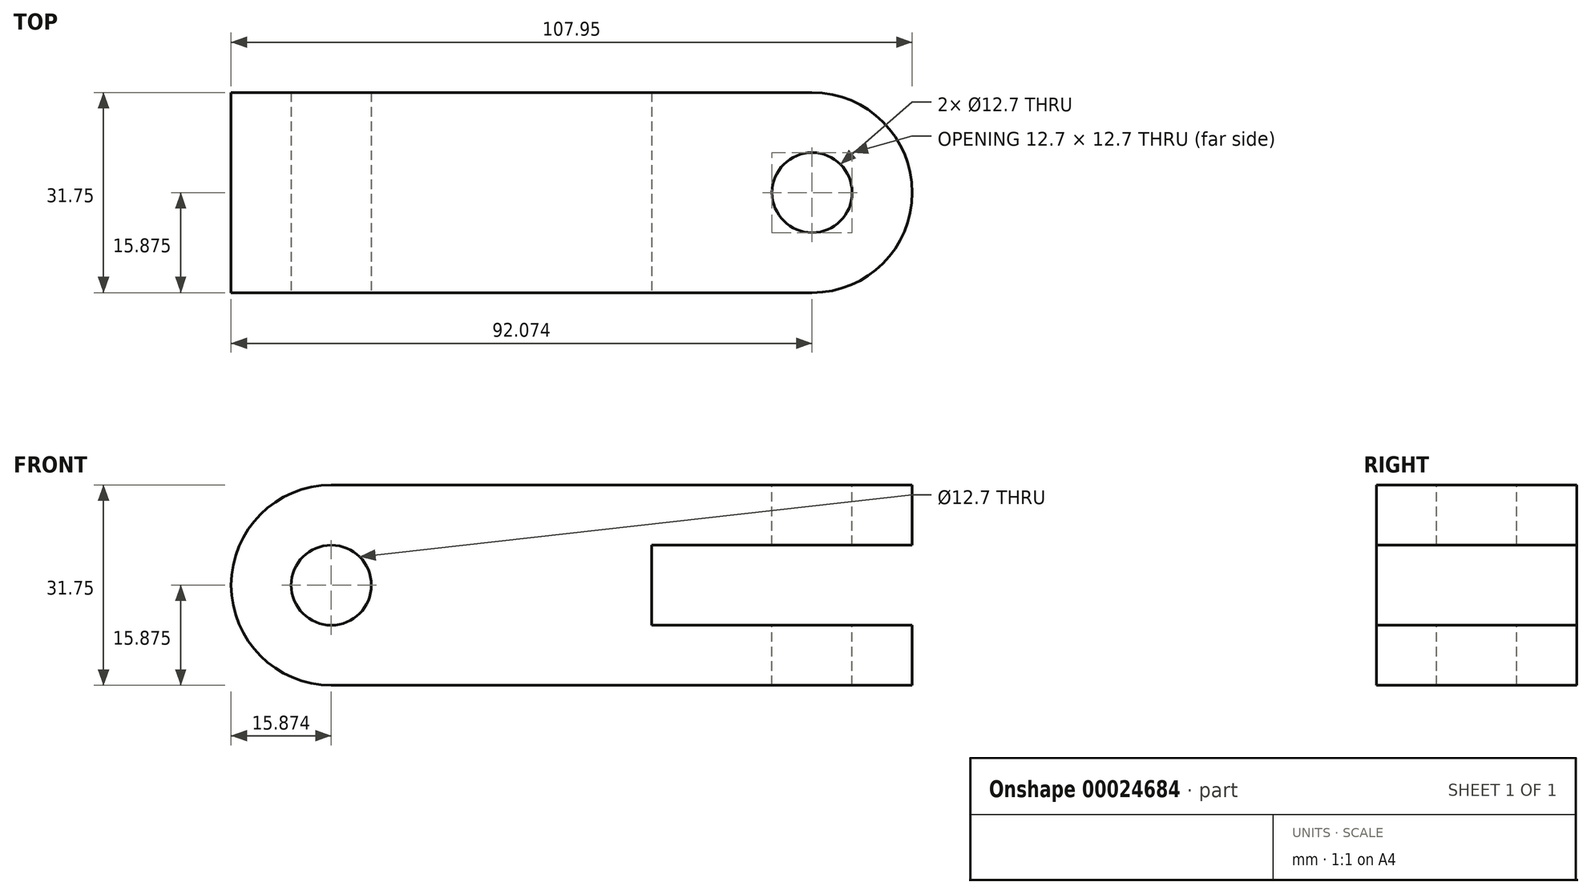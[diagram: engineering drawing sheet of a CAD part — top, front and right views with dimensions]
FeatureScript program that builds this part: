
annotation { "Feature Type Name" : "Feature", "Feature Type Description" : "" }
export const myFeature = defineFeature(function(context is Context, id is Id, definition is map)
    precondition{}
    {
        {
            var Q0;
            Q0=qCreatedBy(makeId("Front.planeOp"),FACE);
            var sketch = newSketch(context, id + "F0", { "sketchPlane" : qUnion([Q0])});
            skLineSegment(sketch, "E0.bottom", {"start": v(-42.47, 14.22) * mm, "end": v(65.48, 14.22) * mm});
            skLineSegment(sketch, "E0.top", {"start": v(-42.47, -17.53) * mm, "end": v(65.48, -17.53) * mm});
            skLineSegment(sketch, "E0.left", {"start": v(-42.47, 14.22) * mm, "end": v(-42.47, -17.53) * mm});
            skLineSegment(sketch, "E0.right", {"start": v(65.48, 14.22) * mm, "end": v(65.48, -17.53) * mm});
            skSolve(sketch);
        }
        {
            var Q0;
            Q0 = qSketchRegion(id + "F0", true);
            extrude(context, id + "F1", {"entities" : qUnion([Q0]), "depth" : 31.75 * mm});
        }
        {
            var Q0;
            Q0=makeQuery(id+"F1.opExtrude","CAP_FACE",FACE,{"disambiguationData":[OSD([sQuery(id+"F0.wireOp",EDGE,"E0.bottom"),sQuery(id+"F0.wireOp",EDGE,"E0.top"),sQuery(id+"F0.wireOp",EDGE,"E0.left"),sQuery(id+"F0.wireOp",EDGE,"E0.right")])],"isStart":false});
            var sketch = newSketch(context, id + "F2", { "sketchPlane" : qUnion([Q0])});
            skArc(sketch, "E1", {"start": v(-26.6, 14.22) * mm, "mid": v(-42.47, -1.66) * mm, "end": v(-26.6, -17.53) * mm});
            skCircle(sketch, "E2", {"center": v(-26.6, -1.66) * mm, "radius": 6.35 * mm});
            skLineSegment(sketch, "E3.0", {"start": v(24.2, 4.7) * mm, "end": v(24.2, -8) * mm});
            skLineSegment(sketch, "E4.trimOffspring", {"start": v(24.2, 4.7) * mm, "end": v(65.48, 4.7) * mm});
            skLineSegment(sketch, "E5.trimOffspring", {"start": v(24.2, -8) * mm, "end": v(65.48, -8) * mm});
            skSolve(sketch);
        }
        {
            var Q0;
            {var subQ1=sQuery(id+"F2.wireOp",EDGE,"E1");var subQ3=makeQuery(id+"F1.opExtrude","CAP_EDGE",EDGE,{"disambiguationData":[OSD([sQuery(id+"F0.wireOp",EDGE,"E0.top")])],"isStart":false});var subQ5=makeQuery(id+"F2.imprint","INTERSECT",VERTEX,{"derivedFrom":[subQ3,subQ1]});Q0=makeQuery(id+"F2.imprint","IMPRINT",FACE,{"disambiguationData":[TD([[makeQuery(id+"F2.imprint","IMPRINT",EDGE,{"disambiguationData":[TD([[subQ5,1.0]])],"derivedFrom":subQ1}),-1.0]])]});}
            var Q1;
            {var subQ1=sQuery(id+"F2.wireOp",EDGE,"E1");var subQ3=makeQuery(id+"F1.opExtrude","CAP_EDGE",EDGE,{"disambiguationData":[OSD([sQuery(id+"F0.wireOp",EDGE,"E0.bottom")])],"isStart":false});var subQ5=makeQuery(id+"F2.imprint","INTERSECT",VERTEX,{"derivedFrom":[subQ3,subQ1]});Q1=makeQuery(id+"F2.imprint","IMPRINT",FACE,{"disambiguationData":[TD([[makeQuery(id+"F2.imprint","IMPRINT",EDGE,{"disambiguationData":[TD([[subQ5,-1.0]])],"derivedFrom":subQ1}),-1.0]])]});}
            var Q2;
            Q2=makeQuery(id+"F2.imprint","IMPRINT",FACE,{"disambiguationData":[TD([[makeQuery(id+"F2.imprint","IMPRINT",EDGE,{"derivedFrom":sQuery(id+"F2.wireOp",EDGE,"E3.0")}),1.0]])]});
            var Q3;
            Q3=makeQuery(id+"F2.imprint","IMPRINT",FACE,{"disambiguationData":[TD([[makeQuery(id+"F2.imprint","IMPRINT",EDGE,{"derivedFrom":sQuery(id+"F2.wireOp",EDGE,"E2")}),1.0]])]});
            extrude(context, id + "F3", {"entities" : qUnion([Q0, Q1, Q2, Q3]), "operationType" : NewBodyOperationType.REMOVE, "endBound" : BoundingType.THROUGH_ALL, "oppositeDirection" : true, "depth" : 25.4 * mm});
        }
        {
            var Q0;
            Q0=makeQuery(id+"F1.opExtrude","SWEPT_FACE",FACE,{"disambiguationData":[OSD([sQuery(id+"F0.wireOp",EDGE,"E0.bottom")])]});
            var sketch = newSketch(context, id + "F4", { "sketchPlane" : qUnion([Q0])});
            skArc(sketch, "E6", {"start": v(49.6, -31.75) * mm, "mid": v(65.48, -15.88) * mm, "end": v(49.6, 0) * mm});
            skLineSegment(sketch, "E7.0", {"start": v(65.48, 0) * mm, "end": v(-26.6, 0) * mm});
            skLineSegment(sketch, "E7.1", {"start": v(65.48, -31.75) * mm, "end": v(65.48, 0) * mm});
            skLineSegment(sketch, "E7.2", {"start": v(-26.6, -31.75) * mm, "end": v(65.48, -31.75) * mm});
            skLineSegment(sketch, "E7.3", {"start": v(-26.6, 0) * mm, "end": v(-26.6, -31.75) * mm});
            skCircle(sketch, "E8", {"center": v(49.6, -15.88) * mm, "radius": 6.35 * mm});
            skSolve(sketch);
        }
        {
            var Q0;
            {var subQ1=sQuery(id+"F4.wireOp",EDGE,"E6");var subQ3=sQuery(id+"F4.wireOp",EDGE,"E7.0");var subQ5=makeQuery(id+"F4.imprint","INTERSECT",VERTEX,{"derivedFrom":[subQ1,subQ3]});Q0=makeQuery(id+"F4.imprint","IMPRINT",FACE,{"disambiguationData":[TD([[makeQuery(id+"F4.imprint","IMPRINT",EDGE,{"disambiguationData":[TD([[subQ5,1.0]])],"derivedFrom":subQ1}),-1.0]])]});}
            var Q1;
            Q1=makeQuery(id+"F4.imprint","IMPRINT",FACE,{"disambiguationData":[TD([[makeQuery(id+"F4.imprint","IMPRINT",EDGE,{"derivedFrom":sQuery(id+"F4.wireOp",EDGE,"E8")}),1.0]])]});
            var Q2;
            {var subQ0=sQuery(id+"F4.wireOp",EDGE,"E7.2");var subQ1=sQuery(id+"F4.wireOp",EDGE,"E6");var subQ2=makeQuery(id+"F4.imprint","INTERSECT",VERTEX,{"derivedFrom":[subQ1,subQ0]});Q2=makeQuery(id+"F4.imprint","IMPRINT",FACE,{"disambiguationData":[TD([[makeQuery(id+"F4.imprint","IMPRINT",EDGE,{"disambiguationData":[TD([[subQ2,-1.0]])],"derivedFrom":subQ1}),-1.0]])]});}
            extrude(context, id + "F5", {"entities" : qUnion([Q0, Q1, Q2]), "operationType" : NewBodyOperationType.REMOVE, "endBound" : BoundingType.THROUGH_ALL, "oppositeDirection" : true, "depth" : 25.4 * mm});
        }
    });
